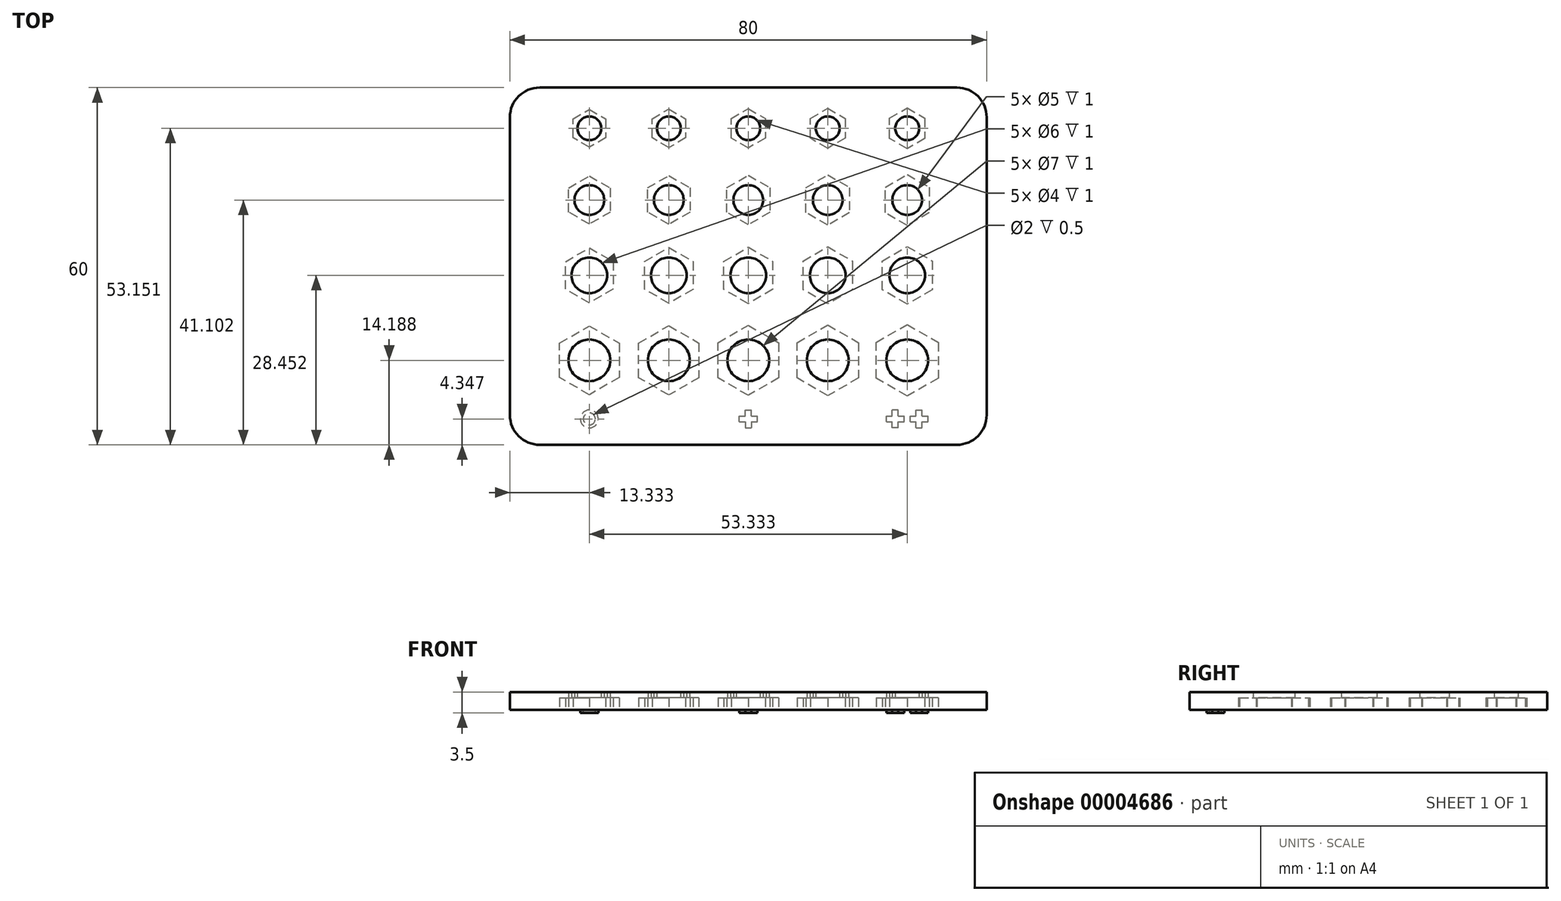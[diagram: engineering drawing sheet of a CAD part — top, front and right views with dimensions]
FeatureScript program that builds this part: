
annotation { "Feature Type Name" : "Feature", "Feature Type Description" : "" }
export const myFeature = defineFeature(function(context is Context, id is Id, definition is map)
    precondition{}
    {
        {
            var Q0;
            Q0=qCreatedBy(makeId("Top.planeOp"),FACE);
            var sketch = newSketch(context, id + "F0", { "sketchPlane" : qUnion([Q0])});
            skLineSegment(sketch, "E0.bottom", {"start": v(0, 0) * mm, "end": v(80, 0) * mm});
            skLineSegment(sketch, "E0.top", {"start": v(0, 60) * mm, "end": v(80, 60) * mm});
            skLineSegment(sketch, "E0.left", {"start": v(0, 0) * mm, "end": v(0, 60) * mm});
            skLineSegment(sketch, "E0.right", {"start": v(80, 0) * mm, "end": v(80, 60) * mm});
            skSolve(sketch);
        }
        {
            var Q0;
            Q0=makeQuery(id+"F0.imprint","IMPRINT",FACE,{"disambiguationData":[TD([[makeQuery(id+"F0.imprint","IMPRINT",EDGE,{"derivedFrom":sQuery(id+"F0.wireOp",EDGE,"E0.bottom")}),1.0]])]});
            extrude(context, id + "F1", {"entities" : qUnion([Q0]), "depth" : 3 * mm});
        }
        {
            var Q0;
            Q0=qCreatedBy(makeId("Top.planeOp"),FACE);
            var sketch = newSketch(context, id + "F2", { "sketchPlane" : qUnion([Q0])});
            skLineSegment(sketch, "E1", {"start": v(0, 53.15) * mm, "end": v(13.33, 53.15) * mm, "construction": true});
            skLineSegment(sketch, "E2", {"start": v(13.33, 53.15) * mm, "end": v(26.67, 53.15) * mm, "construction": true});
            skLineSegment(sketch, "E3", {"start": v(26.67, 53.15) * mm, "end": v(40, 53.15) * mm, "construction": true});
            skLineSegment(sketch, "E4", {"start": v(40, 53.15) * mm, "end": v(53.33, 53.15) * mm, "construction": true});
            skLineSegment(sketch, "E5", {"start": v(53.33, 53.15) * mm, "end": v(66.67, 53.15) * mm, "construction": true});
            skLineSegment(sketch, "E6", {"start": v(66.67, 53.15) * mm, "end": v(80, 53.15) * mm, "construction": true});
            skCircle(sketch, "E7.cCircle", {"center": v(13.33, 53.15) * mm, "radius": 2.75 * mm, "construction": true});
            skLineSegment(sketch, "E7.0", {"start": v(10.58, 54.74) * mm, "end": v(13.33, 56.33) * mm});
            skLineSegment(sketch, "E7.1", {"start": v(13.33, 56.33) * mm, "end": v(16.08, 54.74) * mm});
            skLineSegment(sketch, "E7.2", {"start": v(16.08, 54.74) * mm, "end": v(16.08, 51.56) * mm});
            skLineSegment(sketch, "E7.3", {"start": v(16.08, 51.56) * mm, "end": v(13.33, 49.98) * mm});
            skLineSegment(sketch, "E7.4", {"start": v(13.33, 49.98) * mm, "end": v(10.58, 51.56) * mm});
            skLineSegment(sketch, "E7.5", {"start": v(10.58, 51.56) * mm, "end": v(10.58, 54.74) * mm});
            skPoint(sketch, "E7.0.midPoint", {"position": v(11.96, 55.53) * mm});
            skCircle(sketch, "E8.cCircle", {"center": v(26.67, 53.15) * mm, "radius": 2.8 * mm, "construction": true});
            skLineSegment(sketch, "E8.0", {"start": v(23.87, 54.77) * mm, "end": v(26.67, 56.38) * mm});
            skLineSegment(sketch, "E8.1", {"start": v(26.67, 56.38) * mm, "end": v(29.47, 54.77) * mm});
            skLineSegment(sketch, "E8.2", {"start": v(29.47, 54.77) * mm, "end": v(29.47, 51.53) * mm});
            skLineSegment(sketch, "E8.3", {"start": v(29.47, 51.53) * mm, "end": v(26.67, 49.92) * mm});
            skLineSegment(sketch, "E8.4", {"start": v(26.67, 49.92) * mm, "end": v(23.87, 51.53) * mm});
            skLineSegment(sketch, "E8.5", {"start": v(23.87, 51.53) * mm, "end": v(23.87, 54.77) * mm});
            skPoint(sketch, "E8.0.midPoint", {"position": v(25.27, 55.58) * mm});
            skCircle(sketch, "E9.cCircle", {"center": v(40, 53.15) * mm, "radius": 2.85 * mm, "construction": true});
            skLineSegment(sketch, "E9.0", {"start": v(37.15, 54.8) * mm, "end": v(40, 56.44) * mm});
            skLineSegment(sketch, "E9.1", {"start": v(40, 56.44) * mm, "end": v(42.85, 54.8) * mm});
            skLineSegment(sketch, "E9.2", {"start": v(42.85, 54.8) * mm, "end": v(42.85, 51.5) * mm});
            skLineSegment(sketch, "E9.3", {"start": v(42.85, 51.5) * mm, "end": v(40, 49.86) * mm});
            skLineSegment(sketch, "E9.4", {"start": v(40, 49.86) * mm, "end": v(37.15, 51.5) * mm});
            skLineSegment(sketch, "E9.5", {"start": v(37.15, 51.5) * mm, "end": v(37.15, 54.8) * mm});
            skPoint(sketch, "E9.0.midPoint", {"position": v(38.58, 55.62) * mm});
            skCircle(sketch, "E10.cCircle", {"center": v(53.33, 53.15) * mm, "radius": 2.9 * mm, "construction": true});
            skLineSegment(sketch, "E10.0", {"start": v(50.43, 54.83) * mm, "end": v(53.33, 56.5) * mm});
            skLineSegment(sketch, "E10.1", {"start": v(53.33, 56.5) * mm, "end": v(56.23, 54.83) * mm});
            skLineSegment(sketch, "E10.2", {"start": v(56.23, 54.83) * mm, "end": v(56.23, 51.48) * mm});
            skLineSegment(sketch, "E10.3", {"start": v(56.23, 51.48) * mm, "end": v(53.33, 49.8) * mm});
            skLineSegment(sketch, "E10.4", {"start": v(53.33, 49.8) * mm, "end": v(50.43, 51.48) * mm});
            skLineSegment(sketch, "E10.5", {"start": v(50.43, 51.48) * mm, "end": v(50.43, 54.83) * mm});
            skPoint(sketch, "E10.0.midPoint", {"position": v(51.88, 55.66) * mm});
            skCircle(sketch, "E11.cCircle", {"center": v(66.67, 53.15) * mm, "radius": 2.95 * mm, "construction": true});
            skLineSegment(sketch, "E11.0", {"start": v(63.72, 54.85) * mm, "end": v(66.67, 56.56) * mm});
            skLineSegment(sketch, "E11.1", {"start": v(66.67, 56.56) * mm, "end": v(69.62, 54.85) * mm});
            skLineSegment(sketch, "E11.2", {"start": v(69.62, 54.85) * mm, "end": v(69.62, 51.45) * mm});
            skLineSegment(sketch, "E11.3", {"start": v(69.62, 51.45) * mm, "end": v(66.67, 49.74) * mm});
            skLineSegment(sketch, "E11.4", {"start": v(66.67, 49.74) * mm, "end": v(63.72, 51.45) * mm});
            skLineSegment(sketch, "E11.5", {"start": v(63.72, 51.45) * mm, "end": v(63.72, 54.85) * mm});
            skPoint(sketch, "E11.0.midPoint", {"position": v(65.2, 55.7) * mm});
            skLineSegment(sketch, "E12", {"start": v(0, 28.45) * mm, "end": v(13.33, 28.45) * mm, "construction": true});
            skLineSegment(sketch, "E13", {"start": v(13.33, 28.45) * mm, "end": v(26.67, 28.45) * mm, "construction": true});
            skLineSegment(sketch, "E14", {"start": v(26.67, 28.45) * mm, "end": v(40, 28.45) * mm, "construction": true});
            skLineSegment(sketch, "E15", {"start": v(40, 28.45) * mm, "end": v(53.33, 28.45) * mm, "construction": true});
            skLineSegment(sketch, "E16", {"start": v(53.33, 28.45) * mm, "end": v(66.67, 28.45) * mm, "construction": true});
            skLineSegment(sketch, "E17", {"start": v(66.67, 28.45) * mm, "end": v(80, 28.45) * mm, "construction": true});
            skCircle(sketch, "E18.cCircle", {"center": v(13.33, 28.45) * mm, "radius": 4 * mm, "construction": true});
            skLineSegment(sketch, "E18.0", {"start": v(9.33, 30.76) * mm, "end": v(13.33, 33.07) * mm});
            skLineSegment(sketch, "E18.1", {"start": v(13.33, 33.07) * mm, "end": v(17.33, 30.76) * mm});
            skLineSegment(sketch, "E18.2", {"start": v(17.33, 30.76) * mm, "end": v(17.33, 26.14) * mm});
            skLineSegment(sketch, "E18.3", {"start": v(17.33, 26.14) * mm, "end": v(13.33, 23.83) * mm});
            skLineSegment(sketch, "E18.4", {"start": v(13.33, 23.83) * mm, "end": v(9.33, 26.14) * mm});
            skLineSegment(sketch, "E18.5", {"start": v(9.33, 26.14) * mm, "end": v(9.33, 30.76) * mm});
            skPoint(sketch, "E18.0.midPoint", {"position": v(11.33, 31.92) * mm});
            skCircle(sketch, "E19.cCircle", {"center": v(26.67, 28.45) * mm, "radius": 4.05 * mm, "construction": true});
            skLineSegment(sketch, "E19.0", {"start": v(22.62, 30.8) * mm, "end": v(26.67, 33.13) * mm});
            skLineSegment(sketch, "E19.1", {"start": v(26.67, 33.13) * mm, "end": v(30.72, 30.8) * mm});
            skLineSegment(sketch, "E19.2", {"start": v(30.72, 30.8) * mm, "end": v(30.72, 26.11) * mm});
            skLineSegment(sketch, "E19.3", {"start": v(30.72, 26.11) * mm, "end": v(26.67, 23.78) * mm});
            skLineSegment(sketch, "E19.4", {"start": v(26.67, 23.78) * mm, "end": v(22.62, 26.11) * mm});
            skLineSegment(sketch, "E19.5", {"start": v(22.62, 26.11) * mm, "end": v(22.62, 30.8) * mm});
            skPoint(sketch, "E19.0.midPoint", {"position": v(24.64, 31.96) * mm});
            skCircle(sketch, "E20.cCircle", {"center": v(40, 28.45) * mm, "radius": 4.1 * mm, "construction": true});
            skLineSegment(sketch, "E20.0", {"start": v(35.9, 30.82) * mm, "end": v(40, 33.19) * mm});
            skLineSegment(sketch, "E20.1", {"start": v(40, 33.19) * mm, "end": v(44.1, 30.82) * mm});
            skLineSegment(sketch, "E20.2", {"start": v(44.1, 30.82) * mm, "end": v(44.1, 26.08) * mm});
            skLineSegment(sketch, "E20.3", {"start": v(44.1, 26.08) * mm, "end": v(40, 23.72) * mm});
            skLineSegment(sketch, "E20.4", {"start": v(40, 23.72) * mm, "end": v(35.9, 26.08) * mm});
            skLineSegment(sketch, "E20.5", {"start": v(35.9, 26.08) * mm, "end": v(35.9, 30.82) * mm});
            skPoint(sketch, "E20.0.midPoint", {"position": v(37.95, 32) * mm});
            skCircle(sketch, "E21.cCircle", {"center": v(53.33, 28.45) * mm, "radius": 4.15 * mm, "construction": true});
            skLineSegment(sketch, "E21.0", {"start": v(49.18, 30.85) * mm, "end": v(53.33, 33.24) * mm});
            skLineSegment(sketch, "E21.1", {"start": v(53.33, 33.24) * mm, "end": v(57.48, 30.85) * mm});
            skLineSegment(sketch, "E21.2", {"start": v(57.48, 30.85) * mm, "end": v(57.48, 26.06) * mm});
            skLineSegment(sketch, "E21.3", {"start": v(57.48, 26.06) * mm, "end": v(53.33, 23.66) * mm});
            skLineSegment(sketch, "E21.4", {"start": v(53.33, 23.66) * mm, "end": v(49.18, 26.06) * mm});
            skLineSegment(sketch, "E21.5", {"start": v(49.18, 26.06) * mm, "end": v(49.18, 30.85) * mm});
            skPoint(sketch, "E21.0.midPoint", {"position": v(51.26, 32.05) * mm});
            skCircle(sketch, "E22.cCircle", {"center": v(66.67, 28.45) * mm, "radius": 4.2 * mm, "construction": true});
            skLineSegment(sketch, "E22.0", {"start": v(62.47, 30.88) * mm, "end": v(66.67, 33.3) * mm});
            skLineSegment(sketch, "E22.1", {"start": v(66.67, 33.3) * mm, "end": v(70.87, 30.88) * mm});
            skLineSegment(sketch, "E22.2", {"start": v(70.87, 30.88) * mm, "end": v(70.87, 26.03) * mm});
            skLineSegment(sketch, "E22.3", {"start": v(70.87, 26.03) * mm, "end": v(66.67, 23.6) * mm});
            skLineSegment(sketch, "E22.4", {"start": v(66.67, 23.6) * mm, "end": v(62.47, 26.03) * mm});
            skLineSegment(sketch, "E22.5", {"start": v(62.47, 26.03) * mm, "end": v(62.47, 30.88) * mm});
            skPoint(sketch, "E22.0.midPoint", {"position": v(64.57, 32.09) * mm});
            skLineSegment(sketch, "E23", {"start": v(0, 41.1) * mm, "end": v(13.33, 41.1) * mm, "construction": true});
            skLineSegment(sketch, "E24", {"start": v(13.33, 41.1) * mm, "end": v(26.67, 41.1) * mm, "construction": true});
            skLineSegment(sketch, "E25", {"start": v(26.67, 41.1) * mm, "end": v(40, 41.1) * mm, "construction": true});
            skLineSegment(sketch, "E26", {"start": v(40, 41.1) * mm, "end": v(53.33, 41.1) * mm, "construction": true});
            skLineSegment(sketch, "E27", {"start": v(53.33, 41.1) * mm, "end": v(66.67, 41.1) * mm, "construction": true});
            skLineSegment(sketch, "E28", {"start": v(66.67, 41.1) * mm, "end": v(80, 41.1) * mm, "construction": true});
            skCircle(sketch, "E29.cCircle", {"center": v(13.33, 41.1) * mm, "radius": 3.5 * mm, "construction": true});
            skLineSegment(sketch, "E29.0", {"start": v(9.83, 43.12) * mm, "end": v(13.33, 45.14) * mm});
            skLineSegment(sketch, "E29.1", {"start": v(13.33, 45.14) * mm, "end": v(16.83, 43.12) * mm});
            skLineSegment(sketch, "E29.2", {"start": v(16.83, 43.12) * mm, "end": v(16.83, 39.08) * mm});
            skLineSegment(sketch, "E29.3", {"start": v(16.83, 39.08) * mm, "end": v(13.33, 37.06) * mm});
            skLineSegment(sketch, "E29.4", {"start": v(13.33, 37.06) * mm, "end": v(9.83, 39.08) * mm});
            skLineSegment(sketch, "E29.5", {"start": v(9.83, 39.08) * mm, "end": v(9.83, 43.12) * mm});
            skPoint(sketch, "E29.0.midPoint", {"position": v(11.58, 44.13) * mm});
            skCircle(sketch, "E30.cCircle", {"center": v(26.67, 41.1) * mm, "radius": 3.55 * mm, "construction": true});
            skLineSegment(sketch, "E30.0", {"start": v(23.12, 43.15) * mm, "end": v(26.67, 45.2) * mm});
            skLineSegment(sketch, "E30.1", {"start": v(26.67, 45.2) * mm, "end": v(30.22, 43.15) * mm});
            skLineSegment(sketch, "E30.2", {"start": v(30.22, 43.15) * mm, "end": v(30.22, 39.05) * mm});
            skLineSegment(sketch, "E30.3", {"start": v(30.22, 39.05) * mm, "end": v(26.67, 37) * mm});
            skLineSegment(sketch, "E30.4", {"start": v(26.67, 37) * mm, "end": v(23.12, 39.05) * mm});
            skLineSegment(sketch, "E30.5", {"start": v(23.12, 39.05) * mm, "end": v(23.12, 43.15) * mm});
            skPoint(sketch, "E30.0.midPoint", {"position": v(24.9, 44.18) * mm});
            skCircle(sketch, "E31.cCircle", {"center": v(40, 41.1) * mm, "radius": 3.6 * mm, "construction": true});
            skLineSegment(sketch, "E31.0", {"start": v(36.4, 43.18) * mm, "end": v(40, 45.26) * mm});
            skLineSegment(sketch, "E31.1", {"start": v(40, 45.26) * mm, "end": v(43.6, 43.18) * mm});
            skLineSegment(sketch, "E31.2", {"start": v(43.6, 43.18) * mm, "end": v(43.6, 39.02) * mm});
            skLineSegment(sketch, "E31.3", {"start": v(43.6, 39.02) * mm, "end": v(40, 36.95) * mm});
            skLineSegment(sketch, "E31.4", {"start": v(40, 36.95) * mm, "end": v(36.4, 39.02) * mm});
            skLineSegment(sketch, "E31.5", {"start": v(36.4, 39.02) * mm, "end": v(36.4, 43.18) * mm});
            skPoint(sketch, "E31.0.midPoint", {"position": v(38.2, 44.22) * mm});
            skCircle(sketch, "E32.cCircle", {"center": v(53.33, 41.1) * mm, "radius": 3.65 * mm, "construction": true});
            skLineSegment(sketch, "E32.0", {"start": v(49.68, 43.2) * mm, "end": v(53.33, 45.32) * mm});
            skLineSegment(sketch, "E32.1", {"start": v(53.33, 45.32) * mm, "end": v(56.98, 43.2) * mm});
            skLineSegment(sketch, "E32.2", {"start": v(56.98, 43.2) * mm, "end": v(56.98, 39) * mm});
            skLineSegment(sketch, "E32.3", {"start": v(56.98, 39) * mm, "end": v(53.33, 36.89) * mm});
            skLineSegment(sketch, "E32.4", {"start": v(53.33, 36.89) * mm, "end": v(49.68, 39) * mm});
            skLineSegment(sketch, "E32.5", {"start": v(49.68, 39) * mm, "end": v(49.68, 43.2) * mm});
            skPoint(sketch, "E32.0.midPoint", {"position": v(51.5, 44.26) * mm});
            skCircle(sketch, "E33.cCircle", {"center": v(66.67, 41.1) * mm, "radius": 3.7 * mm, "construction": true});
            skLineSegment(sketch, "E33.0", {"start": v(62.97, 43.24) * mm, "end": v(66.67, 45.37) * mm});
            skLineSegment(sketch, "E33.1", {"start": v(66.67, 45.37) * mm, "end": v(70.37, 43.24) * mm});
            skLineSegment(sketch, "E33.2", {"start": v(70.37, 43.24) * mm, "end": v(70.37, 38.97) * mm});
            skLineSegment(sketch, "E33.3", {"start": v(70.37, 38.97) * mm, "end": v(66.67, 36.83) * mm});
            skLineSegment(sketch, "E33.4", {"start": v(66.67, 36.83) * mm, "end": v(62.97, 38.97) * mm});
            skLineSegment(sketch, "E33.5", {"start": v(62.97, 38.97) * mm, "end": v(62.97, 43.24) * mm});
            skPoint(sketch, "E33.0.midPoint", {"position": v(64.82, 44.3) * mm});
            skLineSegment(sketch, "E34", {"start": v(0, 14.19) * mm, "end": v(13.33, 14.19) * mm, "construction": true});
            skLineSegment(sketch, "E35", {"start": v(13.33, 14.19) * mm, "end": v(26.67, 14.19) * mm, "construction": true});
            skLineSegment(sketch, "E36", {"start": v(26.67, 14.19) * mm, "end": v(40, 14.19) * mm, "construction": true});
            skLineSegment(sketch, "E37", {"start": v(40, 14.19) * mm, "end": v(53.33, 14.19) * mm, "construction": true});
            skLineSegment(sketch, "E38", {"start": v(53.33, 14.19) * mm, "end": v(66.67, 14.19) * mm, "construction": true});
            skLineSegment(sketch, "E39", {"start": v(66.67, 14.19) * mm, "end": v(80, 14.19) * mm, "construction": true});
            skCircle(sketch, "E40.cCircle", {"center": v(13.33, 14.19) * mm, "radius": 5 * mm, "construction": true});
            skLineSegment(sketch, "E40.0", {"start": v(8.33, 17.07) * mm, "end": v(13.33, 19.96) * mm});
            skLineSegment(sketch, "E40.1", {"start": v(13.33, 19.96) * mm, "end": v(18.33, 17.07) * mm});
            skLineSegment(sketch, "E40.2", {"start": v(18.33, 17.07) * mm, "end": v(18.33, 11.3) * mm});
            skLineSegment(sketch, "E40.3", {"start": v(18.33, 11.3) * mm, "end": v(13.33, 8.41) * mm});
            skLineSegment(sketch, "E40.4", {"start": v(13.33, 8.41) * mm, "end": v(8.33, 11.3) * mm});
            skLineSegment(sketch, "E40.5", {"start": v(8.33, 11.3) * mm, "end": v(8.33, 17.07) * mm});
            skPoint(sketch, "E40.0.midPoint", {"position": v(10.83, 18.52) * mm});
            skCircle(sketch, "E41.cCircle", {"center": v(26.67, 14.19) * mm, "radius": 5.05 * mm, "construction": true});
            skLineSegment(sketch, "E41.0", {"start": v(21.62, 17.1) * mm, "end": v(26.67, 20.02) * mm});
            skLineSegment(sketch, "E41.1", {"start": v(26.67, 20.02) * mm, "end": v(31.72, 17.1) * mm});
            skLineSegment(sketch, "E41.2", {"start": v(31.72, 17.1) * mm, "end": v(31.72, 11.27) * mm});
            skLineSegment(sketch, "E41.3", {"start": v(31.72, 11.27) * mm, "end": v(26.67, 8.36) * mm});
            skLineSegment(sketch, "E41.4", {"start": v(26.67, 8.36) * mm, "end": v(21.62, 11.27) * mm});
            skLineSegment(sketch, "E41.5", {"start": v(21.62, 11.27) * mm, "end": v(21.62, 17.1) * mm});
            skPoint(sketch, "E41.0.midPoint", {"position": v(24.14, 18.56) * mm});
            skCircle(sketch, "E42.cCircle", {"center": v(40, 14.19) * mm, "radius": 5.1 * mm, "construction": true});
            skLineSegment(sketch, "E42.0", {"start": v(34.9, 17.13) * mm, "end": v(40, 20.08) * mm});
            skLineSegment(sketch, "E42.1", {"start": v(40, 20.08) * mm, "end": v(45.1, 17.13) * mm});
            skLineSegment(sketch, "E42.2", {"start": v(45.1, 17.13) * mm, "end": v(45.1, 11.24) * mm});
            skLineSegment(sketch, "E42.3", {"start": v(45.1, 11.24) * mm, "end": v(40, 8.3) * mm});
            skLineSegment(sketch, "E42.4", {"start": v(40, 8.3) * mm, "end": v(34.9, 11.24) * mm});
            skLineSegment(sketch, "E42.5", {"start": v(34.9, 11.24) * mm, "end": v(34.9, 17.13) * mm});
            skPoint(sketch, "E42.0.midPoint", {"position": v(37.45, 18.6) * mm});
            skCircle(sketch, "E43.cCircle", {"center": v(53.33, 14.19) * mm, "radius": 5.15 * mm, "construction": true});
            skLineSegment(sketch, "E43.0", {"start": v(48.18, 17.16) * mm, "end": v(53.33, 20.13) * mm});
            skLineSegment(sketch, "E43.1", {"start": v(53.33, 20.13) * mm, "end": v(58.48, 17.16) * mm});
            skLineSegment(sketch, "E43.2", {"start": v(58.48, 17.16) * mm, "end": v(58.48, 11.21) * mm});
            skLineSegment(sketch, "E43.3", {"start": v(58.48, 11.21) * mm, "end": v(53.33, 8.24) * mm});
            skLineSegment(sketch, "E43.4", {"start": v(53.33, 8.24) * mm, "end": v(48.18, 11.21) * mm});
            skLineSegment(sketch, "E43.5", {"start": v(48.18, 11.21) * mm, "end": v(48.18, 17.16) * mm});
            skPoint(sketch, "E43.0.midPoint", {"position": v(50.76, 18.65) * mm});
            skCircle(sketch, "E44.cCircle", {"center": v(66.67, 14.19) * mm, "radius": 5.2 * mm, "construction": true});
            skLineSegment(sketch, "E44.0", {"start": v(61.47, 17.19) * mm, "end": v(66.67, 20.2) * mm});
            skLineSegment(sketch, "E44.1", {"start": v(66.67, 20.2) * mm, "end": v(71.87, 17.19) * mm});
            skLineSegment(sketch, "E44.2", {"start": v(71.87, 17.19) * mm, "end": v(71.87, 11.19) * mm});
            skLineSegment(sketch, "E44.3", {"start": v(71.87, 11.19) * mm, "end": v(66.67, 8.18) * mm});
            skLineSegment(sketch, "E44.4", {"start": v(66.67, 8.18) * mm, "end": v(61.47, 11.19) * mm});
            skLineSegment(sketch, "E44.5", {"start": v(61.47, 11.19) * mm, "end": v(61.47, 17.19) * mm});
            skPoint(sketch, "E44.0.midPoint", {"position": v(64.07, 18.7) * mm});
            skSolve(sketch);
        }
        {
            var Q0;
            Q0 = qSketchRegion(id + "F2", true);
            extrude(context, id + "F3", {"entities" : qUnion([Q0]), "operationType" : NewBodyOperationType.REMOVE, "depth" : 2 * mm});
        }
        {
            var Q0;
            Q0=makeQuery(id+"F0.imprint","IMPRINT",FACE,{"disambiguationData":[TD([[makeQuery(id+"F0.imprint","IMPRINT",EDGE,{"derivedFrom":sQuery(id+"F0.wireOp",EDGE,"E0.bottom")}),1.0]])]});
            var sketch = newSketch(context, id + "F4", { "sketchPlane" : qUnion([Q0])});
            skLineSegment(sketch, "E45", {"start": v(0, 4.35) * mm, "end": v(13.33, 4.35) * mm, "construction": true});
            skLineSegment(sketch, "E46", {"start": v(66.67, 4.35) * mm, "end": v(80, 4.35) * mm, "construction": true});
            skLineSegment(sketch, "E47", {"start": v(13.33, 4.35) * mm, "end": v(40, 4.35) * mm, "construction": true});
            skLineSegment(sketch, "E48", {"start": v(40, 4.35) * mm, "end": v(66.67, 4.35) * mm, "construction": true});
            skCircle(sketch, "E49", {"center": v(13.33, 4.35) * mm, "radius": 1.5 * mm});
            skCircle(sketch, "E50", {"center": v(13.33, 4.35) * mm, "radius": 1 * mm});
            skLineSegment(sketch, "E51.bottom", {"start": v(38.5, 3.85) * mm, "end": v(39.5, 3.85) * mm});
            skLineSegment(sketch, "E51.top", {"start": v(38.5, 4.85) * mm, "end": v(39.5, 4.85) * mm});
            skLineSegment(sketch, "E51.left", {"start": v(38.5, 3.85) * mm, "end": v(38.5, 4.85) * mm});
            skLineSegment(sketch, "E52.top", {"start": v(39.5, 2.85) * mm, "end": v(40.5, 2.85) * mm});
            skLineSegment(sketch, "E52.left", {"start": v(39.5, 3.85) * mm, "end": v(39.5, 2.85) * mm});
            skLineSegment(sketch, "E52.right", {"start": v(40.5, 3.85) * mm, "end": v(40.5, 2.85) * mm});
            skLineSegment(sketch, "E53.bottom", {"start": v(40.5, 3.85) * mm, "end": v(41.5, 3.85) * mm});
            skLineSegment(sketch, "E53.top", {"start": v(40.5, 4.85) * mm, "end": v(41.5, 4.85) * mm});
            skLineSegment(sketch, "E53.right", {"start": v(41.5, 3.85) * mm, "end": v(41.5, 4.85) * mm});
            skLineSegment(sketch, "E54.top", {"start": v(39.5, 5.85) * mm, "end": v(40.5, 5.85) * mm});
            skLineSegment(sketch, "E54.left", {"start": v(39.5, 4.85) * mm, "end": v(39.5, 5.85) * mm});
            skLineSegment(sketch, "E54.right", {"start": v(40.5, 4.85) * mm, "end": v(40.5, 5.85) * mm});
            skLineSegment(sketch, "E55", {"start": v(39.5, 3.85) * mm, "end": v(40.5, 4.85) * mm, "construction": true});
            skLineSegment(sketch, "E56.bottom", {"start": v(65.17, 2.85) * mm, "end": v(64.17, 2.85) * mm});
            skLineSegment(sketch, "E56.top", {"start": v(65.17, 5.85) * mm, "end": v(64.17, 5.85) * mm});
            skLineSegment(sketch, "E56.left", {"start": v(65.17, 2.85) * mm, "end": v(65.17, 3.85) * mm});
            skLineSegment(sketch, "E56.right", {"start": v(64.17, 2.85) * mm, "end": v(64.17, 3.85) * mm});
            skLineSegment(sketch, "E57.bottom", {"start": v(63.17, 3.85) * mm, "end": v(64.17, 3.85) * mm});
            skLineSegment(sketch, "E57.top", {"start": v(63.17, 4.85) * mm, "end": v(64.17, 4.85) * mm});
            skLineSegment(sketch, "E57.left", {"start": v(63.17, 3.85) * mm, "end": v(63.17, 4.85) * mm});
            skLineSegment(sketch, "E57.right", {"start": v(66.17, 3.85) * mm, "end": v(66.17, 4.85) * mm});
            skLineSegment(sketch, "E58.bottom", {"start": v(68.17, 2.85) * mm, "end": v(69.17, 2.85) * mm});
            skLineSegment(sketch, "E58.top", {"start": v(68.17, 5.85) * mm, "end": v(69.17, 5.85) * mm});
            skLineSegment(sketch, "E58.left", {"start": v(68.17, 2.85) * mm, "end": v(68.17, 3.85) * mm});
            skLineSegment(sketch, "E58.right", {"start": v(69.17, 2.85) * mm, "end": v(69.17, 3.85) * mm});
            skLineSegment(sketch, "E59.bottom", {"start": v(67.17, 3.85) * mm, "end": v(68.17, 3.85) * mm});
            skLineSegment(sketch, "E59.top", {"start": v(67.17, 4.85) * mm, "end": v(68.17, 4.85) * mm});
            skLineSegment(sketch, "E59.left", {"start": v(67.17, 3.85) * mm, "end": v(67.17, 4.85) * mm});
            skLineSegment(sketch, "E59.right", {"start": v(70.17, 3.85) * mm, "end": v(70.17, 4.85) * mm});
            skLineSegment(sketch, "E60.trimOffspring", {"start": v(64.17, 4.85) * mm, "end": v(64.17, 5.85) * mm});
            skLineSegment(sketch, "E61.trimOffspring", {"start": v(65.17, 3.85) * mm, "end": v(66.17, 3.85) * mm});
            skLineSegment(sketch, "E62.trimOffspring", {"start": v(65.17, 4.85) * mm, "end": v(65.17, 5.85) * mm});
            skLineSegment(sketch, "E63.trimOffspring", {"start": v(65.17, 4.85) * mm, "end": v(66.17, 4.85) * mm});
            skLineSegment(sketch, "E64.trimOffspring", {"start": v(68.17, 4.85) * mm, "end": v(68.17, 5.85) * mm});
            skLineSegment(sketch, "E65.trimOffspring", {"start": v(69.17, 3.85) * mm, "end": v(70.17, 3.85) * mm});
            skLineSegment(sketch, "E66.trimOffspring", {"start": v(69.17, 4.85) * mm, "end": v(69.17, 5.85) * mm});
            skLineSegment(sketch, "E67.trimOffspring", {"start": v(69.17, 4.85) * mm, "end": v(70.17, 4.85) * mm});
            skLineSegment(sketch, "E68", {"start": v(64.17, 3.85) * mm, "end": v(65.17, 4.85) * mm, "construction": true});
            skLineSegment(sketch, "E69", {"start": v(68.17, 3.85) * mm, "end": v(69.17, 4.85) * mm, "construction": true});
            skLineSegment(sketch, "E70", {"start": v(64.67, 4.35) * mm, "end": v(68.67, 4.35) * mm, "construction": true});
            skSolve(sketch);
        }
        {
            var Q0;
            Q0=makeQuery(id+"F4.imprint","IMPRINT",FACE,{"disambiguationData":[TD([[makeQuery(id+"F4.imprint","IMPRINT",EDGE,{"derivedFrom":sQuery(id+"F4.wireOp",EDGE,"E49")}),1.0]])]});
            var Q1;
            Q1=makeQuery(id+"F4.imprint","IMPRINT",FACE,{"disambiguationData":[TD([[makeQuery(id+"F4.imprint","IMPRINT",EDGE,{"derivedFrom":sQuery(id+"F4.wireOp",EDGE,"E56.bottom")}),-1.0]])]});
            var Q2;
            Q2=makeQuery(id+"F4.imprint","IMPRINT",FACE,{"disambiguationData":[TD([[makeQuery(id+"F4.imprint","IMPRINT",EDGE,{"derivedFrom":sQuery(id+"F4.wireOp",EDGE,"E58.bottom")}),1.0]])]});
            var Q3;
            Q3=makeQuery(id+"F4.imprint","IMPRINT",FACE,{"disambiguationData":[TD([[makeQuery(id+"F4.imprint","IMPRINT",EDGE,{"derivedFrom":sQuery(id+"F4.wireOp",EDGE,"E51.bottom")}),1.0]])]});
            extrude(context, id + "F5", {"entities" : qUnion([Q0, Q1, Q2, Q3]), "operationType" : NewBodyOperationType.ADD, "oppositeDirection" : true, "depth" : 0.5 * mm});
        }
        {
            var Q0;
            Q0=makeQuery(id+"F0.imprint","IMPRINT",FACE,{"disambiguationData":[TD([[makeQuery(id+"F0.imprint","IMPRINT",EDGE,{"derivedFrom":sQuery(id+"F0.wireOp",EDGE,"E0.bottom")}),1.0]])]});
            var sketch = newSketch(context, id + "F6", { "sketchPlane" : qUnion([Q0])});
            skCircle(sketch, "E71", {"center": v(13.33, 14.19) * mm, "radius": 3.5 * mm});
            skCircle(sketch, "E72", {"center": v(26.67, 14.19) * mm, "radius": 3.5 * mm});
            skCircle(sketch, "E73", {"center": v(40, 14.19) * mm, "radius": 3.5 * mm});
            skCircle(sketch, "E74", {"center": v(53.33, 14.19) * mm, "radius": 3.5 * mm});
            skCircle(sketch, "E75", {"center": v(66.67, 14.19) * mm, "radius": 3.5 * mm});
            skCircle(sketch, "E76", {"center": v(13.33, 28.45) * mm, "radius": 3 * mm});
            skCircle(sketch, "E77", {"center": v(26.67, 28.45) * mm, "radius": 3 * mm});
            skCircle(sketch, "E78", {"center": v(40, 28.45) * mm, "radius": 3 * mm});
            skCircle(sketch, "E79", {"center": v(53.33, 28.45) * mm, "radius": 3 * mm});
            skCircle(sketch, "E80", {"center": v(66.67, 28.45) * mm, "radius": 3 * mm});
            skCircle(sketch, "E81", {"center": v(13.33, 41.1) * mm, "radius": 2.5 * mm});
            skCircle(sketch, "E82", {"center": v(26.67, 41.1) * mm, "radius": 2.5 * mm});
            skCircle(sketch, "E83", {"center": v(40, 41.1) * mm, "radius": 2.5 * mm});
            skCircle(sketch, "E84", {"center": v(53.33, 41.1) * mm, "radius": 2.5 * mm});
            skCircle(sketch, "E85", {"center": v(66.67, 41.1) * mm, "radius": 2.5 * mm});
            skCircle(sketch, "E86", {"center": v(13.33, 53.15) * mm, "radius": 2 * mm});
            skCircle(sketch, "E87", {"center": v(26.67, 53.15) * mm, "radius": 2 * mm});
            skCircle(sketch, "E88", {"center": v(40, 53.15) * mm, "radius": 2 * mm});
            skCircle(sketch, "E89", {"center": v(53.33, 53.15) * mm, "radius": 2 * mm});
            skCircle(sketch, "E90", {"center": v(66.67, 53.15) * mm, "radius": 2 * mm});
            skSolve(sketch);
        }
        {
            var Q0;
            Q0 = qSketchRegion(id + "F6", true);
            extrude(context, id + "F7", {"entities" : qUnion([Q0]), "operationType" : NewBodyOperationType.REMOVE, "endBound" : BoundingType.THROUGH_ALL, "depth" : 25 * mm});
        }
        {
            var Q0;
            Q0=makeQuery(id+"F1.opExtrude","SWEPT_EDGE",EDGE,{"disambiguationData":[OSD([sQuery(id+"F0.wireOp",EDGE,"E0.bottom"),sQuery(id+"F0.wireOp",EDGE,"E0.left")])]});
            var Q1;
            Q1=makeQuery(id+"F1.opExtrude","SWEPT_EDGE",EDGE,{"disambiguationData":[OSD([sQuery(id+"F0.wireOp",EDGE,"E0.bottom"),sQuery(id+"F0.wireOp",EDGE,"E0.right")])]});
            var Q2;
            Q2=makeQuery(id+"F1.opExtrude","SWEPT_EDGE",EDGE,{"disambiguationData":[OSD([sQuery(id+"F0.wireOp",EDGE,"E0.top"),sQuery(id+"F0.wireOp",EDGE,"E0.right")])]});
            var Q3;
            Q3=makeQuery(id+"F1.opExtrude","SWEPT_EDGE",EDGE,{"disambiguationData":[OSD([sQuery(id+"F0.wireOp",EDGE,"E0.top"),sQuery(id+"F0.wireOp",EDGE,"E0.left")])]});
            fillet(context, id + "F8", {"entities" : qUnion([Q0, Q1, Q2, Q3]), "radius" : 5 * mm, "tangentPropagation" : true, "allowEdgeOverflow" : false});
        }
    });
